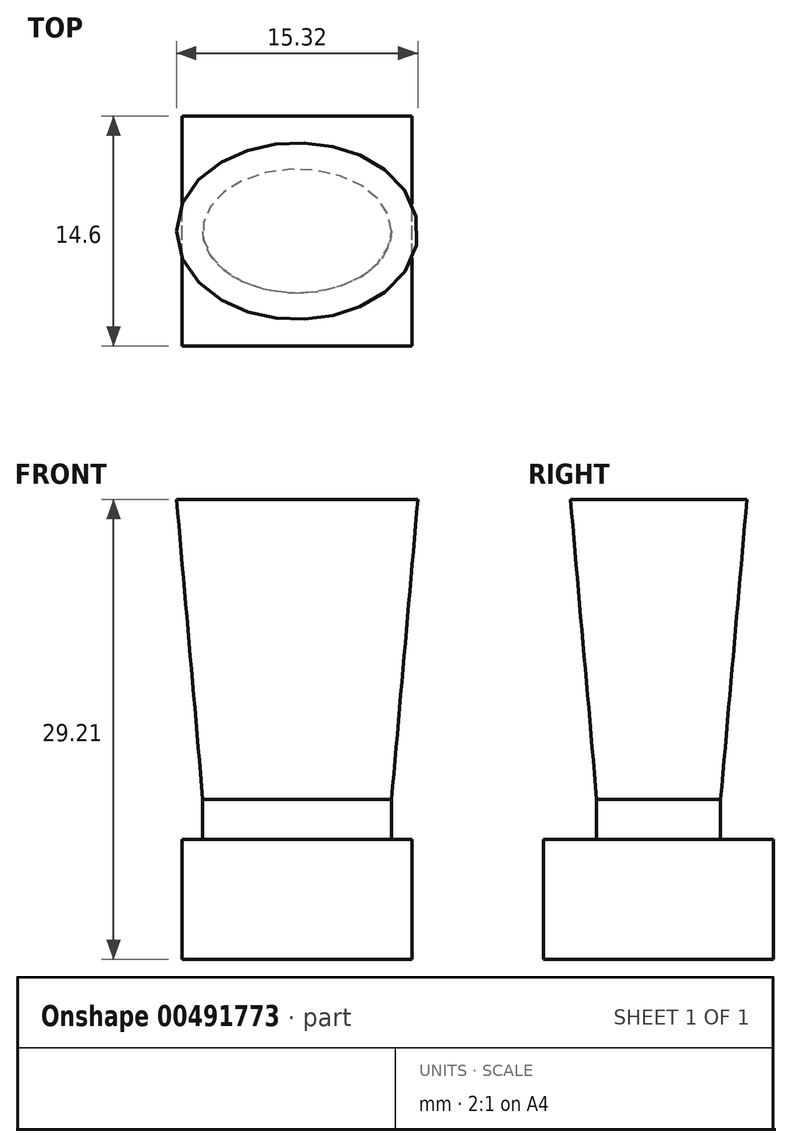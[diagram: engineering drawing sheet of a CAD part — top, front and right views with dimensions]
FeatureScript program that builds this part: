
annotation { "Feature Type Name" : "Feature", "Feature Type Description" : "" }
export const myFeature = defineFeature(function(context is Context, id is Id, definition is map)
    precondition{}
    {
        {
            var Q0;
            Q0=qCreatedBy(makeId("Top.planeOp"),FACE);
            var sketch = newSketch(context, id + "F0", { "sketchPlane" : qUnion([Q0])});
            skLineSegment(sketch, "E0.bottom", {"start": v(7.3, -7.3) * mm, "end": v(-7.3, -7.3) * mm});
            skLineSegment(sketch, "E0.top", {"start": v(7.3, 7.3) * mm, "end": v(-7.3, 7.3) * mm});
            skLineSegment(sketch, "E0.left", {"start": v(7.3, -7.3) * mm, "end": v(7.3, 7.3) * mm});
            skLineSegment(sketch, "E0.right", {"start": v(-7.3, -7.3) * mm, "end": v(-7.3, 7.3) * mm});
            skPoint(sketch, "E0.middle", {"position": v(0, 0) * mm});
            skSolve(sketch);
        }
        {
            var Q0;
            Q0=makeQuery(id+"F0.imprint","IMPRINT",FACE,{"disambiguationData":[TD([[makeQuery(id+"F0.imprint","IMPRINT",EDGE,{"derivedFrom":sQuery(id+"F0.wireOp",EDGE,"E0.bottom")}),-1.0]])]});
            extrude(context, id + "F1", {"entities" : qUnion([Q0]), "depth" : 7.62 * mm});
        }
        {
            var Q0;
            Q0=makeQuery(id+"F1.opExtrude","CAP_FACE",FACE,{"disambiguationData":[OSD([sQuery(id+"F0.wireOp",EDGE,"E0.bottom"),sQuery(id+"F0.wireOp",EDGE,"E0.top"),sQuery(id+"F0.wireOp",EDGE,"E0.left"),sQuery(id+"F0.wireOp",EDGE,"E0.right")])],"isStart":false});
            var sketch = newSketch(context, id + "F2", { "sketchPlane" : qUnion([Q0])});
            skEllipse(sketch, "E1", {"center": v(0, 0) * mm, "majorRadius": 6 * mm, "minorRadius": 3.94 * mm, "majorAxis": v(1, 0)});
            skSolve(sketch);
        }
        {
            var Q0;
            Q0=makeQuery(id+"F2.imprint","IMPRINT",FACE,{"disambiguationData":[TD([[makeQuery(id+"F2.imprint","IMPRINT",EDGE,{"derivedFrom":sQuery(id+"F2.wireOp",EDGE,"E1")}),1.0]])]});
            extrude(context, id + "F3", {"entities" : qUnion([Q0]), "operationType" : NewBodyOperationType.ADD, "depth" : 2.54 * mm});
        }
        {
            var Q0;
            Q0=makeQuery(id+"F3.opExtrude","CAP_FACE",FACE,{"disambiguationData":[OSD([sQuery(id+"F2.wireOp",EDGE,"E1")])],"isStart":false});
            var sketch = newSketch(context, id + "F4", { "sketchPlane" : qUnion([Q0])});
            skFitSpline(sketch, "E2.0", {"points": [v(7.15, -1.15) * mm, v(7.32, 0) * mm, v(7.15, 1.15) * mm, v(6.66, 2.2) * mm, v(5.9, 3.12) * mm, v(4.96, 3.87) * mm, v(3.86, 4.46) * mm, v(2.64, 4.9) * mm, v(1.34, 5.15) * mm, v(0, 5.24) * mm, v(-1.34, 5.15) * mm, v(-2.64, 4.9) * mm, v(-3.86, 4.46) * mm, v(-4.96, 3.87) * mm, v(-5.9, 3.12) * mm, v(-6.66, 2.2) * mm, v(-7.15, 1.15) * mm, v(-7.32, 0) * mm, v(-7.15, -1.15) * mm, v(-6.66, -2.2) * mm, v(-5.9, -3.12) * mm, v(-4.96, -3.87) * mm, v(-3.86, -4.46) * mm, v(-2.64, -4.9) * mm, v(-1.34, -5.15) * mm, v(0, -5.24) * mm, v(1.34, -5.15) * mm, v(2.64, -4.9) * mm, v(3.86, -4.46) * mm, v(4.96, -3.87) * mm, v(5.9, -3.12) * mm, v(6.66, -2.2) * mm, v(7.15, -1.15) * mm, v(7.32, 0) * mm, v(7.15, 1.15) * mm, v(7.15, -1.15) * mm]});
            skSolve(sketch);
        }
        {
            var Q0;
            Q0=makeQuery(id+"F4.imprint","IMPRINT",FACE,{"disambiguationData":[TD([[makeQuery(id+"F4.imprint","IMPRINT",EDGE,{"derivedFrom":makeQuery(id+"F3.opExtrude","CAP_EDGE",EDGE,{"disambiguationData":[OSD([sQuery(id+"F2.wireOp",EDGE,"E1")])],"isStart":false})}),1.0]])]});
            var Q1;
            Q1=makeQuery(id+"F4.imprint","IMPRINT",FACE,{"disambiguationData":[TD([[makeQuery(id+"F4.imprint","IMPRINT",EDGE,{"derivedFrom":sQuery(id+"F4.wireOp",EDGE,"E2.0")}),1.0]])]});
            extrude(context, id + "F5", {"entities" : qUnion([Q0, Q1]), "operationType" : NewBodyOperationType.ADD, "depth" : 19.05 * mm, "hasDraft" : true, "draftAngle" : 5 * degree});
        }
    });
